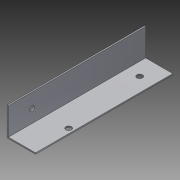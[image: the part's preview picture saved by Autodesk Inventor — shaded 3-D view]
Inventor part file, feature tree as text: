
AUTODESK INVENTOR PART (.ipt)
format: ipt  version: 2014 SP1 (Build 180222100, 222)  size: 97,792 bytes
history: native  units: in
note: dims shown in document units (in); Inventor stores cm internally (conversion verified against a paired STEP export)
features: extrude x3, sketch x3
ambient origin geometry x8: Origin, YZ Plane, XZ Plane, XY Plane, X Axis, Y Axis, Z Axis, Center Point
bodies: Solid1 (feature_tree)
feature tree (6):
  extrude  "Extrusion1"  Depth=0.0312in
  extrude  "Extrusion2"  Depth=3.625in
  extrude  "Extrusion3"  Depth=0.625in
  sketch  "Sketch1"  dims[d0=0.75in d1=0.0312in]
  sketch  "Sketch2"  dims[d2=3.625in d3=0.0in d4=0.125in]
  sketch  "Sketch3"  dims[d5=0.15in d6=1.0in d7=0.5in d8=1.0in d9=0.0in d10=0.125in d11=0.625in d12=1.0in d13=0.0in]
